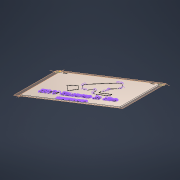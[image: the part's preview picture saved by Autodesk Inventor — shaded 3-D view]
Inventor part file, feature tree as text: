
AUTODESK INVENTOR PART (.ipt)
format: ipt  version: 2021 (Build 250183000, 183)  size: 5,317,632 bytes
history: native  units: mm
features: other x5, extrude x4, sketch x3, fillet x2
ambient origin geometry x8: Origin, YZ Plane, XZ Plane, XY Plane, X Axis, Y Axis, Z Axis, Center Point
bodies: Solid1 (feature_tree), Solid2 (feature_tree)
feature tree (14):
  other  "Blocks"
  sketch  "Sketch1"  dims[d2=250.0mm d3=190.0mm]
  extrude  "Extrusion1"  Depth=190.0mm
  extrude  "Extrusion2"  Depth=0.6mm TaperAngle=0.0deg
  extrude  "Extrusion3"  Depth=10.0mm
  extrude  "Extrusion4"  Depth=5.0mm
  fillet  "Fillet1"  Radius=3.0mm
  fillet  "Fillet2"  Radius=10.0mm
  other  "cctv"
  other  "pls"
  sketch  "Sketch2"  dims[d4=3.0mm d5=0.0mm d6=0.6mm d7=0.0mm]
  sketch  "Sketch3"  dims[d8=0.6mm d9=0.0mm d10=10.0mm d11=3.0mm d12=3.0mm d13=10.0mm d14=20.0mm d16=220.0mm d17=10.0mm d19=10.0mm d21=0.0mm d22=0.0mm d23=1.5mm d24=5.0mm]
  other  "cctv:1"
  other  "pls:1"
